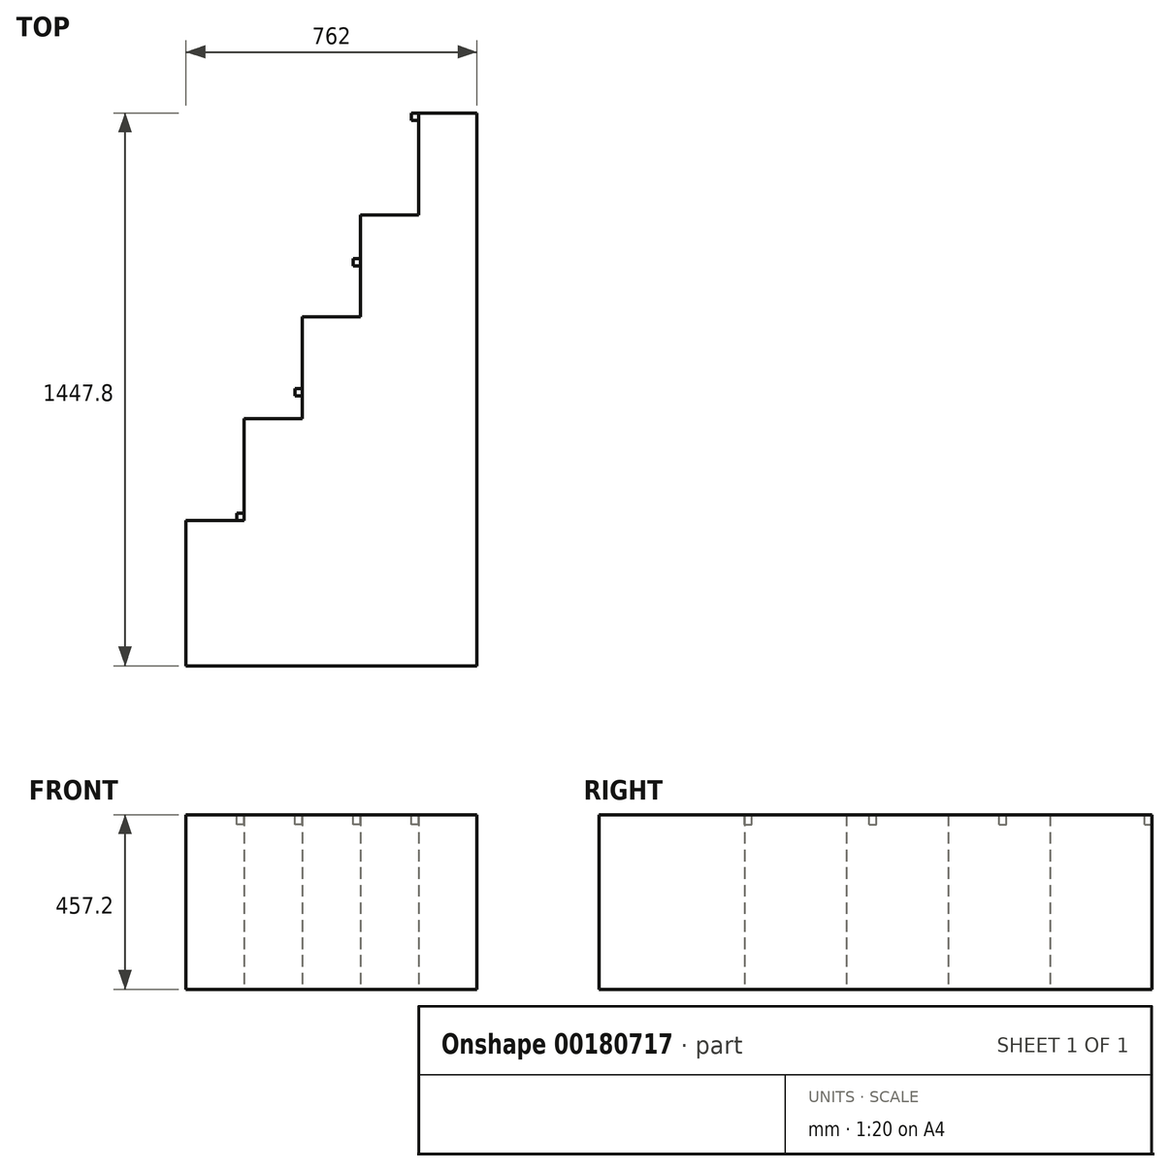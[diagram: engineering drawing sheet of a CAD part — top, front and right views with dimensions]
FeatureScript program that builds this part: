
annotation { "Feature Type Name" : "Feature", "Feature Type Description" : "" }
export const myFeature = defineFeature(function(context is Context, id is Id, definition is map)
    precondition{}
    {
        {
            var Q0;
            Q0=qCreatedBy(makeId("Top.planeOp"),FACE);
            var sketch = newSketch(context, id + "F0", { "sketchPlane" : qUnion([Q0])});
            skLineSegment(sketch, "E0.bottom", {"start": v(-1076.34, -402.7) * mm, "end": v(-923.94, -402.7) * mm});
            skLineSegment(sketch, "E0.top", {"start": v(-1076.34, -783.7) * mm, "end": v(-923.94, -783.7) * mm});
            skLineSegment(sketch, "E0.left", {"start": v(-1076.34, -402.7) * mm, "end": v(-1076.34, -783.7) * mm});
            skLineSegment(sketch, "E0.right", {"start": v(-923.94, -402.7) * mm, "end": v(-923.94, -783.7) * mm});
            skLineSegment(sketch, "E1", {"start": v(-923.94, -402.7) * mm, "end": v(-923.94, -136) * mm});
            skLineSegment(sketch, "E2", {"start": v(-923.94, -136) * mm, "end": v(-771.54, -136) * mm});
            skLineSegment(sketch, "E3", {"start": v(-771.54, -136) * mm, "end": v(-771.54, -783.7) * mm});
            skLineSegment(sketch, "E4", {"start": v(-771.54, -783.7) * mm, "end": v(-923.94, -783.7) * mm});
            skLineSegment(sketch, "E5", {"start": v(-771.54, -136) * mm, "end": v(-771.54, 130.7) * mm});
            skLineSegment(sketch, "E6", {"start": v(-771.54, 130.7) * mm, "end": v(-619.14, 130.7) * mm});
            skLineSegment(sketch, "E7", {"start": v(-619.14, 130.7) * mm, "end": v(-619.14, -783.7) * mm});
            skLineSegment(sketch, "E8", {"start": v(-619.14, -783.7) * mm, "end": v(-771.54, -783.7) * mm});
            skLineSegment(sketch, "E9", {"start": v(-619.14, 130.7) * mm, "end": v(-619.14, 397.4) * mm});
            skLineSegment(sketch, "E10", {"start": v(-619.14, 397.4) * mm, "end": v(-466.74, 397.4) * mm});
            skLineSegment(sketch, "E11", {"start": v(-466.74, 397.4) * mm, "end": v(-466.74, -783.7) * mm});
            skLineSegment(sketch, "E12", {"start": v(-466.74, -783.7) * mm, "end": v(-619.14, -783.7) * mm});
            skLineSegment(sketch, "E13", {"start": v(-466.74, 397.4) * mm, "end": v(-466.74, 664.1) * mm});
            skLineSegment(sketch, "E14", {"start": v(-466.74, 664.1) * mm, "end": v(-314.34, 664.1) * mm});
            skLineSegment(sketch, "E15", {"start": v(-314.34, 664.1) * mm, "end": v(-314.34, -783.7) * mm});
            skLineSegment(sketch, "E16", {"start": v(-314.34, -783.7) * mm, "end": v(-466.74, -783.7) * mm});
            skSolve(sketch);
        }
        {
            var Q0;
            Q0=makeQuery(id+"F0.imprint","IMPRINT",FACE,{"disambiguationData":[TD([[makeQuery(id+"F0.imprint","IMPRINT",EDGE,{"derivedFrom":sQuery(id+"F0.wireOp",EDGE,"E11")}),1.0]])]});
            var Q1;
            Q1=makeQuery(id+"F0.imprint","IMPRINT",FACE,{"disambiguationData":[TD([[makeQuery(id+"F0.imprint","IMPRINT",EDGE,{"derivedFrom":sQuery(id+"F0.wireOp",EDGE,"E7")}),1.0]])]});
            var Q2;
            Q2=makeQuery(id+"F0.imprint","IMPRINT",FACE,{"disambiguationData":[TD([[makeQuery(id+"F0.imprint","IMPRINT",EDGE,{"derivedFrom":sQuery(id+"F0.wireOp",EDGE,"E3")}),1.0]])]});
            var Q3;
            Q3=makeQuery(id+"F0.imprint","IMPRINT",FACE,{"disambiguationData":[TD([[makeQuery(id+"F0.imprint","IMPRINT",EDGE,{"derivedFrom":sQuery(id+"F0.wireOp",EDGE,"E0.right")}),1.0]])]});
            var Q4;
            Q4=makeQuery(id+"F0.imprint","IMPRINT",FACE,{"disambiguationData":[TD([[makeQuery(id+"F0.imprint","IMPRINT",EDGE,{"derivedFrom":sQuery(id+"F0.wireOp",EDGE,"E0.bottom")}),-1.0]])]});
            extrude(context, id + "F1", {"entities" : qUnion([Q0, Q1, Q2, Q3, Q4]), "depth" : 457.2 * mm});
        }
        {
            var Q0;
            Q0=makeQuery(id+"F1.opExtrude","CAP_FACE",FACE,{"disambiguationData":[OSD([sQuery(id+"F0.wireOp",EDGE,"E0.bottom"),sQuery(id+"F0.wireOp",EDGE,"E0.top"),sQuery(id+"F0.wireOp",EDGE,"E0.left"),sQuery(id+"F0.wireOp",EDGE,"E1"),sQuery(id+"F0.wireOp",EDGE,"E2"),sQuery(id+"F0.wireOp",EDGE,"E4"),sQuery(id+"F0.wireOp",EDGE,"E5"),sQuery(id+"F0.wireOp",EDGE,"E6"),sQuery(id+"F0.wireOp",EDGE,"E8"),sQuery(id+"F0.wireOp",EDGE,"E9"),sQuery(id+"F0.wireOp",EDGE,"E10"),sQuery(id+"F0.wireOp",EDGE,"E12"),sQuery(id+"F0.wireOp",EDGE,"E13"),sQuery(id+"F0.wireOp",EDGE,"E14"),sQuery(id+"F0.wireOp",EDGE,"E15"),sQuery(id+"F0.wireOp",EDGE,"E16")])],"isStart":false});
            var sketch = newSketch(context, id + "F2", { "sketchPlane" : qUnion([Q0])});
            skLineSegment(sketch, "E17.bottom", {"start": v(-923.94, -402.7) * mm, "end": v(-942.99, -402.7) * mm});
            skLineSegment(sketch, "E17.top", {"start": v(-923.94, -383.66) * mm, "end": v(-942.99, -383.66) * mm});
            skLineSegment(sketch, "E17.left", {"start": v(-923.94, -402.7) * mm, "end": v(-923.94, -383.66) * mm});
            skLineSegment(sketch, "E17.right", {"start": v(-942.99, -402.7) * mm, "end": v(-942.99, -383.66) * mm});
            skLineSegment(sketch, "E18.bottom", {"start": v(-771.54, -76.44) * mm, "end": v(-790.59, -76.44) * mm});
            skLineSegment(sketch, "E18.top", {"start": v(-771.54, -57.39) * mm, "end": v(-790.59, -57.39) * mm});
            skLineSegment(sketch, "E18.left", {"start": v(-771.54, -76.44) * mm, "end": v(-771.54, -57.39) * mm});
            skLineSegment(sketch, "E18.right", {"start": v(-790.59, -76.44) * mm, "end": v(-790.59, -57.39) * mm});
            skLineSegment(sketch, "E19.bottom", {"start": v(-619.14, 264.04) * mm, "end": v(-638.19, 264.04) * mm});
            skLineSegment(sketch, "E19.top", {"start": v(-619.14, 283.1) * mm, "end": v(-638.19, 283.1) * mm});
            skLineSegment(sketch, "E19.left", {"start": v(-619.14, 264.04) * mm, "end": v(-619.14, 283.1) * mm});
            skLineSegment(sketch, "E19.right", {"start": v(-638.19, 264.04) * mm, "end": v(-638.19, 283.1) * mm});
            skLineSegment(sketch, "E20.bottom", {"start": v(-466.74, 664.1) * mm, "end": v(-485.79, 664.1) * mm});
            skLineSegment(sketch, "E20.top", {"start": v(-466.74, 645.04) * mm, "end": v(-485.79, 645.04) * mm});
            skLineSegment(sketch, "E20.left", {"start": v(-466.74, 664.1) * mm, "end": v(-466.74, 645.04) * mm});
            skLineSegment(sketch, "E20.right", {"start": v(-485.79, 664.1) * mm, "end": v(-485.79, 645.04) * mm});
            skSolve(sketch);
        }
        {
            var Q0;
            Q0=makeQuery(id+"F2.imprint","IMPRINT",FACE,{"disambiguationData":[TD([[makeQuery(id+"F2.imprint","IMPRINT",EDGE,{"derivedFrom":sQuery(id+"F2.wireOp",EDGE,"E17.bottom")}),1.0]])]});
            var Q1;
            Q1=makeQuery(id+"F2.imprint","IMPRINT",FACE,{"disambiguationData":[TD([[makeQuery(id+"F2.imprint","IMPRINT",EDGE,{"derivedFrom":sQuery(id+"F2.wireOp",EDGE,"E18.bottom")}),-1.0]])]});
            var Q2;
            Q2=makeQuery(id+"F2.imprint","IMPRINT",FACE,{"disambiguationData":[TD([[makeQuery(id+"F2.imprint","IMPRINT",EDGE,{"derivedFrom":sQuery(id+"F2.wireOp",EDGE,"E19.bottom")}),-1.0]])]});
            var Q3;
            Q3=makeQuery(id+"F2.imprint","IMPRINT",FACE,{"disambiguationData":[TD([[makeQuery(id+"F2.imprint","IMPRINT",EDGE,{"derivedFrom":sQuery(id+"F2.wireOp",EDGE,"E20.bottom")}),1.0]])]});
            extrude(context, id + "F3", {"entities" : qUnion([Q0, Q1, Q2, Q3]), "oppositeDirection" : true, "depth" : 25.4 * mm});
        }
    });
